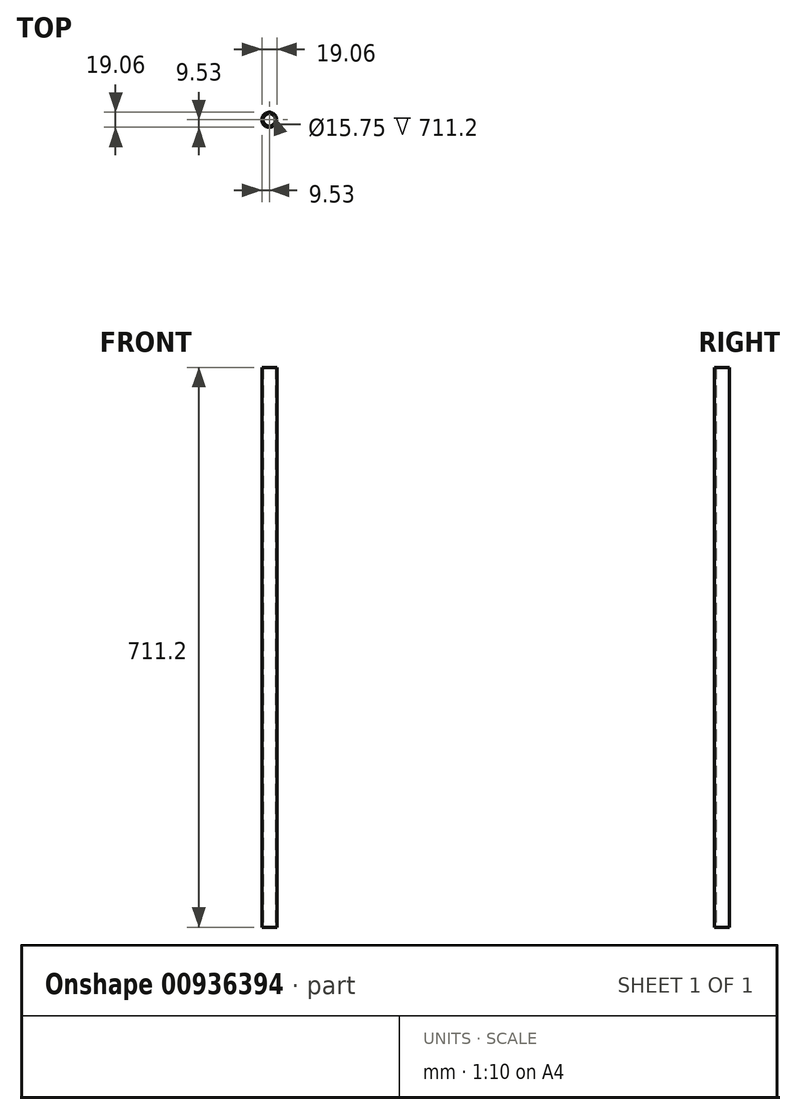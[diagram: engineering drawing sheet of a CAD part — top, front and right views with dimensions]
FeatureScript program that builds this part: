
annotation { "Feature Type Name" : "Feature", "Feature Type Description" : "" }
export const myFeature = defineFeature(function(context is Context, id is Id, definition is map)
    precondition{}
    {
        {
            var Q0;
            Q0=qCreatedBy(makeId("Top.planeOp"),FACE);
            var sketch = newSketch(context, id + "F0", { "sketchPlane" : qUnion([Q0])});
            skCircle(sketch, "E0", {"center": v(0, 0) * mm, "radius": 9.53 * mm});
            skCircle(sketch, "E1", {"center": v(0, 0) * mm, "radius": 7.87 * mm});
            skSolve(sketch);
        }
        {
            var Q0;
            Q0=makeQuery(id+"F0.imprint","IMPRINT",FACE,{"disambiguationData":[TD([[makeQuery(id+"F0.imprint","IMPRINT",EDGE,{"derivedFrom":sQuery(id+"F0.wireOp",EDGE,"E0")}),1.0]])]});
            extrude(context, id + "F1", {"entities" : qUnion([Q0]), "depth" : 711.2 * mm, "offsetDistance" : 25.4 * mm});
        }
    });
